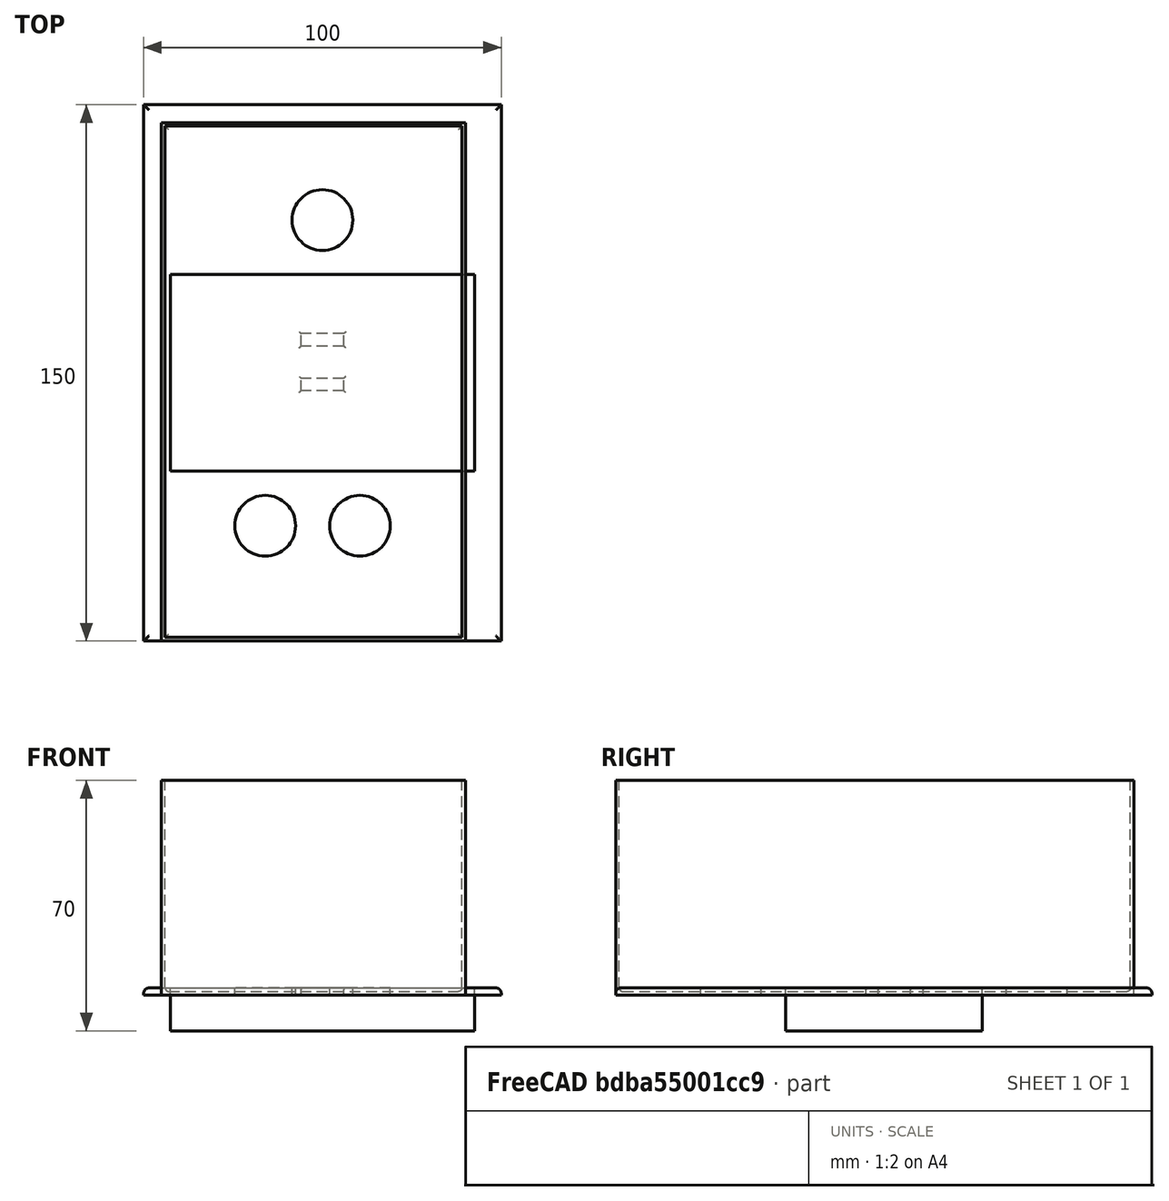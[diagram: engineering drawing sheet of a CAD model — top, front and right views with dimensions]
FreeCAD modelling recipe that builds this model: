
FCSTD DOCUMENT  (FreeCAD 0.16RUnknown)
Label: panel
License: All rights reserved
LicenseURL: http://en.wikipedia.org/wiki/All_rights_reserved
objects: Part::Box×6, Part::Cut×6, Part::Fillet×4, Part::Cylinder×3
note: 19 computed .brp shape members not serialized (recipe doc carries the construction recipe); baked Part::Feature solids carry a one-line shape summary decoded from their .brp

FEATURE [Part::Box] Box  label="Cube"
  Height = 2
  Length = 100
  Placement = pos=(-5,0,0) rot=(0,0,1;0rad)
  Width = 150
FEATURE [Part::Cylinder] Cylinder  label="Taladro boton A"
  Angle = 360
  Height = 10
  Placement = pos=(29,32.25,-4) rot=(0,0,1;0rad)
  Radius = 8.5
FEATURE [Part::Cut] Cut
  Base = -> Box
  Tool = -> Cylinder
FEATURE [Part::Box] Box001  label="Cube001"
  Height = 10
  Length = 12
  Placement = pos=(39,82.5,0) rot=(0,0,1;0rad)
  Width = 3.5
FEATURE [Part::Box] Box002  label="Cube002"
  Height = 10
  Length = 12
  Placement = pos=(39,70,0) rot=(0,0,1;0rad)
  Width = 3.5
FEATURE [Part::Cut] Cut001
  Base = -> Cut
  Tool = -> Box002
FEATURE [Part::Cut] Cut002
  Base = -> Cut001
  Tool = -> Box001
FEATURE [Part::Cylinder] Cylinder001  label="Taladro salida Y"
  Angle = 360
  Height = 10
  Placement = pos=(45,117.75,-4) rot=(0,0,1;0rad)
  Radius = 8.5
FEATURE [Part::Box] Box003  label="Breadboard layout"
  Height = 12
  Length = 85
  Placement = pos=(2.5,47.5,-10) rot=(0,0,1;0rad)
  Width = 55
FEATURE [Part::Cylinder] Cylinder002  label="Taladro boton B"
  Angle = 360
  Height = 10
  Placement = pos=(55.5,32.25,-4) rot=(0,0,1;0rad)
  Radius = 8.5
FEATURE [Part::Cut] Cut003
  Base = -> Cut002
  Tool = -> Cylinder002
FEATURE [Part::Cut] Cut004
  Base = -> Cut003
  Tool = -> Cylinder001
FEATURE [Part::Fillet] Fillet
  Base = -> Cut004
  Edges = 4 edges r=1.5: [Edge2,Edge7,Edge8,Edge9]
FEATURE [Part::Fillet] Fillet001
  Base = -> Fillet
  Edges = 8 edges r=0.5: [Edge33,Edge34,Edge35,Edge36,Edge37,Edge38,Edge39,Edge40]
FEATURE [Part::Box] Box004  label="Cube003"
  Height = 60
  Length = 85
  Width = 145
FEATURE [Part::Box] Box005  label="Cube004"
  Height = 65
  Length = 83
  Placement = pos=(1,1,1) rot=(0,0,1;0rad)
  Width = 143
FEATURE [Part::Cut] Cut005
  Base = -> Box004
  Tool = -> Box005
FEATURE [Part::Fillet] Fillet002
  Base = -> Cut005
  Edges = 4 edges r=1: [Edge19,Edge21,Edge23,Edge24]
FEATURE [Part::Fillet] Fillet003
  Base = -> Cut005
  Edges = 4 edges r=2: [Edge1,Edge3,Edge6,Edge15]
